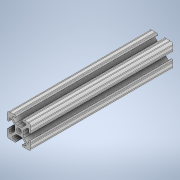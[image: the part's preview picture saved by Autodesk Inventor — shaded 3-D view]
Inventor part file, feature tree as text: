
AUTODESK INVENTOR PART (.ipt)
format: ipt  version: 2020 (Build 240168000, 168)  size: 231,936 bytes
history: native  units: in
note: dims shown in document units (in); Inventor stores cm internally (conversion verified against a paired STEP export)
features: extrude x1, sketch x1
ambient origin geometry x8: Origin, YZ Plane, XZ Plane, XY Plane, X Axis, Y Axis, Z Axis, Center Point
bodies: Solid1 (feature_tree)
feature tree (2):
  extrude  "Extrusion1"  [1 undecoded]
  sketch  "Sketch1"  dims[d0=6.0in d1=0.0in]
note: 1 required parameter value undecoded (feature->parameter linkage not recoverable at this tier; creation-order binding heuristic only, values carry confidence <= 0.55)
